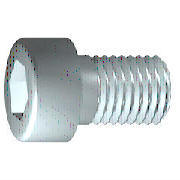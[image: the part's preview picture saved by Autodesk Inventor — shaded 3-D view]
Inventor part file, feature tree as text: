
AUTODESK INVENTOR PART (.ipt)
format: ipt  version: 2013 (Build 170138000, 138)  size: 187,392 bytes
history: native  units: mm (DEFAULTED — no unit token found)
features: sketch x2, extrude x1, plane x1, fillet x1
ambient origin geometry x7: Origin, YZ Plane, XY Plane, X Axis, Y Axis, Z Axis, Center Point
bodies: Solid1 (feature_tree), Body (feature_tree)
feature tree (5):
  extrude  "Slot"  Depth=0.306825mm
  plane  "Work Plane1"
  fillet  "Fillet2"  Radius=3.0mm
  sketch  "Sketch1"  dims[d1=14.693275mm d2=0.306825mm d3=3.0mm]
  sketch  "Sketch2"  dims[d4=1.5mm d5=60.0deg d6=3.0mm d7=3.0mm d8=2.886751mm d9=5.5mm d10=90.0deg d11=10.0mm d12=0.0mm d13=14.693275mm d14=0.0mm d15=0.306725mm d16=0.306725mm d17=0.3mm d19=0.0mm d26=18.0mm d27=45.0deg d28=0.0mm d29=0.0mm d30=0.1mm]
